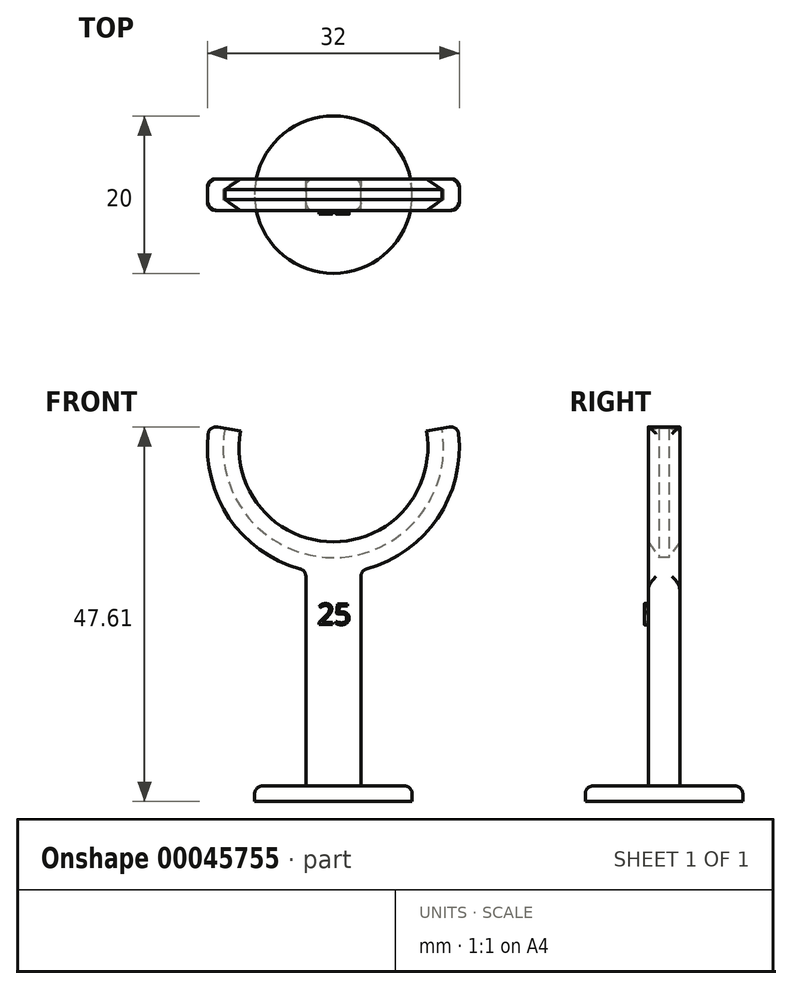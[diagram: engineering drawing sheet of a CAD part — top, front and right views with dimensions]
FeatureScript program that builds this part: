
annotation { "Feature Type Name" : "Feature", "Feature Type Description" : "" }
export const myFeature = defineFeature(function(context is Context, id is Id, definition is map)
    precondition{}
    {
        {
            var Q0;
            Q0=qCreatedBy(makeId("Top.planeOp"),FACE);
            var sketch = newSketch(context, id + "F0", { "sketchPlane" : qUnion([Q0])});
            skCircle(sketch, "E0", {"center": v(0, 0) * mm, "radius": 10 * mm});
            skSolve(sketch);
        }
        {
            var Q0;
            Q0=makeQuery(id+"F0.imprint","IMPRINT",FACE,{"disambiguationData":[TD([[makeQuery(id+"F0.imprint","IMPRINT",EDGE,{"derivedFrom":sQuery(id+"F0.wireOp",EDGE,"E0")}),1.0]])]});
            extrude(context, id + "F1", {"entities" : qUnion([Q0]), "depth" : 2 * mm});
        }
        {
            var Q0;
            Q0=qCreatedBy(makeId("Front.planeOp"),FACE);
            var sketch = newSketch(context, id + "F2", { "sketchPlane" : qUnion([Q0])});
            skLineSegment(sketch, "E1", {"start": v(0, 0) * mm, "end": v(0, 45) * mm, "construction": true});
            skLineSegment(sketch, "E2", {"start": v(-12, 45) * mm, "end": v(12, 45) * mm, "construction": true});
            skCircle(sketch, "E3", {"center": v(0, 45) * mm, "radius": 12 * mm, "construction": true});
            skLineSegment(sketch, "E4", {"start": v(-11.82, 47.08) * mm, "end": v(0, 45) * mm, "construction": true});
            skLineSegment(sketch, "E5", {"start": v(-11.82, 47.08) * mm, "end": v(-15.76, 47.78) * mm});
            skLineSegment(sketch, "E6.MirrorCS", {"start": v(11.82, 47.08) * mm, "end": v(15.76, 47.78) * mm});
            skArc(sketch, "E7", {"start": v(-15.76, 47.78) * mm, "mid": v(0, 29) * mm, "end": v(15.76, 47.78) * mm});
            skArc(sketch, "E8", {"start": v(-11.82, 47.08) * mm, "mid": v(0, 33) * mm, "end": v(11.82, 47.08) * mm});
            skLineSegment(sketch, "E9", {"start": v(-3.5, 29.39) * mm, "end": v(3.5, 29.39) * mm, "construction": true});
            skLineSegment(sketch, "E10.0", {"start": v(-10, 2) * mm, "end": v(10, 2) * mm, "construction": true});
            skLineSegment(sketch, "E11", {"start": v(-3.5, 29.39) * mm, "end": v(-3.5, 2) * mm});
            skLineSegment(sketch, "E12.MirrorCS", {"start": v(3.5, 29.39) * mm, "end": v(3.5, 2) * mm});
            skLineSegment(sketch, "E13", {"start": v(-3.5, 2) * mm, "end": v(3.5, 2) * mm});
            skSolve(sketch);
        }
        {
            var Q0;
            Q0=qSketchRegion(id+"F2",true);
            extrude(context, id + "F3", {"entities" : qUnion([Q0]), "operationType" : NewBodyOperationType.ADD, "endBound" : BoundingType.SYMMETRIC, "depth" : 4 * mm, "hasSecondDirection" : true, "secondDirectionOppositeDirection" : true, "secondDirectionDepth" : 1.5 * mm});
        }
        {
            var Q0;
            Q0=makeQuery(id+"F3.opExtrude","CAP_EDGE",EDGE,{"disambiguationData":[OSD([sQuery(id+"F2.wireOp",EDGE,"E8")])],"isStart":false});
            var Q1;
            Q1=makeQuery(id+"F3.opExtrude","CAP_VERTEX",VERTEX,{"disambiguationData":[OSD([sQuery(id+"F2.wireOp",EDGE,"E5"),sQuery(id+"F2.wireOp",EDGE,"E8")])],"isStart":false});
            cPlane(context, id + "F4", {"entities" : qUnion([Q0, Q1]), "cplaneType" : CPlaneType.CURVE_POINT, "offset" : 150 * mm, "width" : 150 * mm, "height" : 150 * mm});
        }
        {
            var Q0;
            Q0=qCreatedBy(id+"F4.planeOp",FACE);
            var sketch = newSketch(context, id + "F5", { "sketchPlane" : qUnion([Q0])});
            skPoint(sketch, "E14.0", {"position": v(-19.81, 2) * mm});
            skLineSegment(sketch, "E15.0", {"start": v(-19.81, 2) * mm, "end": v(-19.81, -2) * mm});
            skLineSegment(sketch, "E16", {"start": v(-19.81, 0) * mm, "end": v(-21.81, 0) * mm, "construction": true});
            skLineSegment(sketch, "E17", {"start": v(-21.81, 0.65) * mm, "end": v(-21.81, -0.65) * mm});
            skLineSegment(sketch, "E18", {"start": v(-21.81, 0.65) * mm, "end": v(-19.81, 2) * mm});
            skLineSegment(sketch, "E19", {"start": v(-21.81, -0.65) * mm, "end": v(-19.81, -2) * mm});
            skSolve(sketch);
        }
        {
            var Q0;
            Q0=makeQuery(id+"F5.imprint","IMPRINT",FACE,{"disambiguationData":[TD([[makeQuery(id+"F5.imprint","IMPRINT",EDGE,{"derivedFrom":sQuery(id+"F5.wireOp",EDGE,"E15.0")}),-1.0]])]});
            var Q1;
            Q1=makeQuery(id+"F3.opExtrude","CAP_EDGE",EDGE,{"disambiguationData":[OSD([sQuery(id+"F2.wireOp",EDGE,"E8")])],"isStart":false});
            sweep(context, id + "F6", {"operationType" : NewBodyOperationType.REMOVE, "profiles" : qUnion([Q0]), "path" : qUnion([Q1])});
        }
        {
            var Q0;
            {var subQ0=sQuery(id+"F2.wireOp",EDGE,"E7");Q0=makeQuery(id+"F3.opExtrude","SWEPT_FACE",FACE,{"disambiguationData":[OSD([subQ0]),TDD([makeQuery(id+"F2.imprint","IMPRINT",EDGE,{"disambiguationData":[TD([[makeQuery(id+"F2.imprint","INTERSECT",VERTEX,{"derivedFrom":[sQuery(id+"F2.wireOp",EDGE,"E5"),subQ0]}),-1.0]])],"derivedFrom":subQ0})])]});}
            var Q1;
            {var subQ0=sQuery(id+"F2.wireOp",EDGE,"E7");Q1=makeQuery(id+"F3.opExtrude","SWEPT_FACE",FACE,{"disambiguationData":[OSD([subQ0]),TDD([makeQuery(id+"F2.imprint","IMPRINT",EDGE,{"disambiguationData":[TD([[makeQuery(id+"F2.imprint","INTERSECT",VERTEX,{"derivedFrom":[sQuery(id+"F2.wireOp",EDGE,"E6.MirrorCS"),subQ0]}),1.0]])],"derivedFrom":subQ0})])]});}
            var Q2;
            Q2=makeQuery(id+"F3.opExtrude","CAP_EDGE",EDGE,{"disambiguationData":[OSD([sQuery(id+"F2.wireOp",EDGE,"E13")])],"isStart":false});
            var Q3;
            Q3=makeQuery(id+"F1.opExtrude","CAP_EDGE",EDGE,{"disambiguationData":[OSD([sQuery(id+"F0.wireOp",EDGE,"E0")])],"isStart":false});
            fillet(context, id + "F7", {"entities" : qUnion([Q0, Q1, Q2, Q3]), "radius" : 1 * mm, "tangentPropagation" : true, "allowEdgeOverflow" : false});
        }
        {
            var Q0;
            Q0=makeQuery(id+"F3.opExtrude","CAP_FACE",FACE,{"disambiguationData":[OSD([sQuery(id+"F2.wireOp",EDGE,"E5"),sQuery(id+"F2.wireOp",EDGE,"E6.MirrorCS"),sQuery(id+"F2.wireOp",EDGE,"E7"),sQuery(id+"F2.wireOp",EDGE,"E8"),sQuery(id+"F2.wireOp",EDGE,"E11"),sQuery(id+"F2.wireOp",EDGE,"E12.MirrorCS"),sQuery(id+"F2.wireOp",EDGE,"E13")])],"isStart":false});
            var sketch = newSketch(context, id + "F8", { "sketchPlane" : qUnion([Q0])});
            skText(sketch, "E20", { "text": "25", "fontName": "OpenSans-Regular.ttf"});
            skPoint(sketch, "E21.1", {"position": v(0, 0) * mm});
            skLineSegment(sketch, "E22.0", {"start": v(0, 0) * mm, "end": v(0, 45) * mm, "construction": true});
            const initialGuessF8  = {"E20": [-0.002, 0.0225, 1, 0, 0.00265]};
            skSetInitialGuess(sketch, initialGuessF8);
            skSolve(sketch);
        }
        {
            var Q0;
            Q0=qSketchRegion(id+"F8",true);
            extrude(context, id + "F9", {"entities" : qUnion([Q0]), "operationType" : NewBodyOperationType.ADD, "depth" : .5 * mm});
        }
    });
